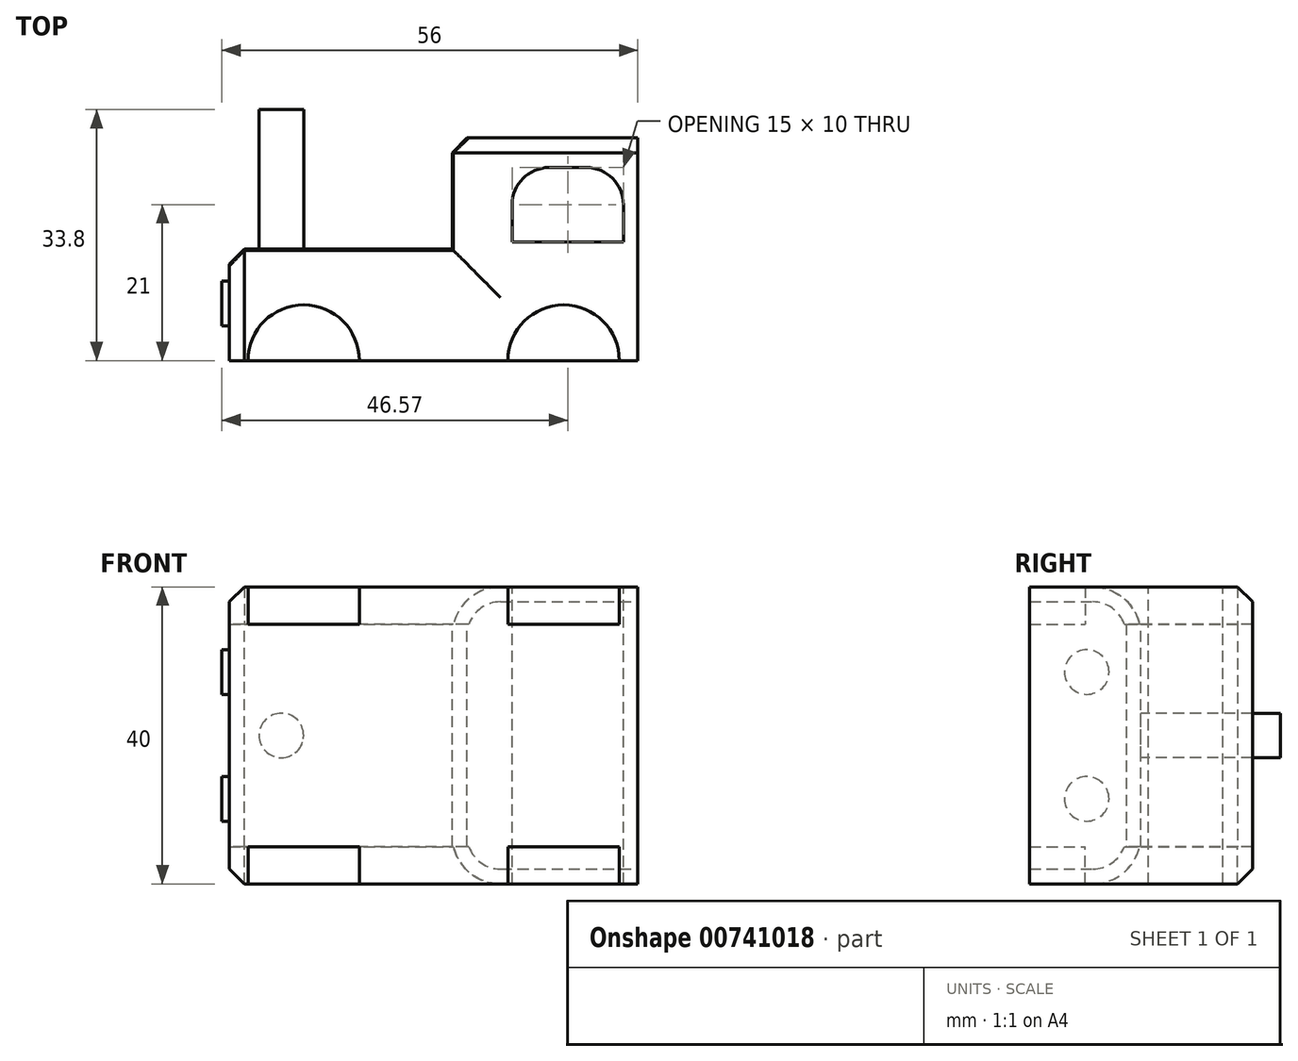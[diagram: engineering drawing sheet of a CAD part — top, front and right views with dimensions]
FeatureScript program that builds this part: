
annotation { "Feature Type Name" : "Feature", "Feature Type Description" : "" }
export const myFeature = defineFeature(function(context is Context, id is Id, definition is map)
    precondition{}
    {
        {
            var Q0;
            Q0=qCreatedBy(makeId("Top.planeOp"),FACE);
            var sketch = newSketch(context, id + "F0", { "sketchPlane" : qUnion([Q0])});
            skLineSegment(sketch, "E0.bottom", {"start": v(27.5, -15) * mm, "end": v(-27.5, -15) * mm});
            skLineSegment(sketch, "E0.top", {"start": v(27.5, 15) * mm, "end": v(-27.5, 15) * mm});
            skLineSegment(sketch, "E0.left", {"start": v(27.5, -15) * mm, "end": v(27.5, 15) * mm});
            skLineSegment(sketch, "E0.right", {"start": v(-27.5, -15) * mm, "end": v(-27.5, 15) * mm});
            skPoint(sketch, "E0.middle", {"position": v(0, 0) * mm});
            skSolve(sketch);
        }
        {
            var Q0;
            Q0 = qSketchRegion(id + "F0", true);
            extrude(context, id + "F1", {"entities" : qUnion([Q0]), "depth" : 30 * mm, "offsetDistance" : 25.4 * mm, "symmetric" : true});
        }
        {
            var Q0;
            Q0=makeQuery(id+"F1.opExtrude","CAP_FACE",FACE,{"disambiguationData":[OSD([sQuery(id+"F0.wireOp",EDGE,"E0.bottom"),sQuery(id+"F0.wireOp",EDGE,"E0.top"),sQuery(id+"F0.wireOp",EDGE,"E0.left"),sQuery(id+"F0.wireOp",EDGE,"E0.right")])],"isStart":false});
            var sketch = newSketch(context, id + "F2", { "sketchPlane" : qUnion([Q0])});
            skLineSegment(sketch, "E1", {"start": v(-27.5, 0) * mm, "end": v(2.5, 0) * mm});
            skLineSegment(sketch, "E2", {"start": v(2.5, 0) * mm, "end": v(2.5, 15) * mm});
            skSolve(sketch);
        }
        {
            var Q0;
            {var subQ0=sQuery(id+"F2.wireOp",EDGE,"E1");Q0=makeQuery(id+"F2.imprint","IMPRINT",FACE,{"disambiguationData":[TD([[makeQuery(id+"F2.imprint","IMPRINT",EDGE,{"derivedFrom":subQ0}),1.0]])]});}
            extrude(context, id + "F3", {"entities" : qUnion([Q0]), "operationType" : NewBodyOperationType.REMOVE, "endBound" : BoundingType.THROUGH_ALL, "oppositeDirection" : true, "depth" : 3.53 * mm, "offsetDistance" : 25.4 * mm});
        }
        {
            var Q0;
            Q0=makeQuery(id+"F1.opExtrude","CAP_FACE",FACE,{"disambiguationData":[OSD([sQuery(id+"F0.wireOp",EDGE,"E0.bottom"),sQuery(id+"F0.wireOp",EDGE,"E0.top"),sQuery(id+"F0.wireOp",EDGE,"E0.left"),sQuery(id+"F0.wireOp",EDGE,"E0.right")])],"isStart":false});
            var sketch = newSketch(context, id + "F4", { "sketchPlane" : qUnion([Q0])});
            skCircle(sketch, "E3", {"center": v(-17.5, -15) * mm, "radius": 7.5 * mm});
            skCircle(sketch, "E4.1.0.0", {"center": v(17.5, -15) * mm, "radius": 7.5 * mm});
            skLineSegment(sketch, "E4.direction1", {"start": v(-17.5, -15) * mm, "end": v(17.5, -15) * mm, "construction": true});
            skSolve(sketch);
        }
        {
            var Q0;
            {var subQ0=makeQuery(id+"F1.opExtrude","CAP_EDGE",EDGE,{"disambiguationData":[OSD([sQuery(id+"F0.wireOp",EDGE,"E0.left")])],"isStart":false});Q0=makeQuery(id+"F4.imprint","IMPRINT",FACE,{"disambiguationData":[TD([[makeQuery(id+"F4.imprint","IMPRINT",EDGE,{"derivedFrom":subQ0}),1.0]])]});}
            extrude(context, id + "F5", {"entities" : qUnion([Q0]), "operationType" : NewBodyOperationType.ADD, "depth" : 5 * mm, "offsetDistance" : 25.4 * mm});
        }
        {
            var Q0;
            Q0=makeQuery(id+"F5.opExtrude","CAP_EDGE",EDGE,{"disambiguationData":[OSD([sQuery(id+"F2.wireOp",EDGE,"E1")])],"isStart":false});
            var Q1;
            Q1=makeQuery(id+"FCjg2uL26yfeYgk_1.1.F5.opExtrude","CAP_EDGE",EDGE,{"disambiguationData":[OSD([sQuery(id+"F2.wireOp",EDGE,"E1")])],"isStart":false});
            var Q2;
            Q2=makeQuery(id+"F5.opExtrude","CAP_EDGE",EDGE,{"disambiguationData":[OSD([sQuery(id+"F2.wireOp",EDGE,"E2")])],"isStart":false});
            var Q3;
            Q3=makeQuery(id+"FCjg2uL26yfeYgk_1.1.F5.opExtrude","CAP_EDGE",EDGE,{"disambiguationData":[OSD([sQuery(id+"F2.wireOp",EDGE,"E2")])],"isStart":false});
            fillet(context, id + "F6", {"entities" : qUnion([Q0, Q1, Q2, Q3]), "radius" : 6.5 * mm, "tangentPropagation" : true, "allowEdgeOverflow" : false});
        }
        {
            var Q0;
            {var subQ0=sQuery(id+"F2.wireOp",EDGE,"E2");var subQ1=sQuery(id+"F0.wireOp",EDGE,"E0.top");Q0=makeQuery(id+"FCjg2uL26yfeYgk_1.1.F5.boolean.opBoolean","MERGE",EDGE,{"derivedFrom":[makeQuery(id+"F5.boolean.opBoolean","MERGE",EDGE,{"derivedFrom":[makeQuery(id+"F3.boolean.opBoolean","COPY",EDGE,{"derivedFrom":makeQuery(id+"F3.opExtrude","SWEPT_EDGE",EDGE,{"disambiguationData":[OSD([subQ1,subQ0])]})}),makeQuery(id+"F5.opExtrude","SWEPT_EDGE",EDGE,{"disambiguationData":[OSD([subQ1,subQ0])]})]}),makeQuery(id+"FCjg2uL26yfeYgk_1.1.F5.opExtrude","SWEPT_EDGE",EDGE,{"disambiguationData":[OSD([subQ1,subQ0])]})]});}
            var Q1;
            {var subQ0=sQuery(id+"F2.wireOp",EDGE,"E1");var subQ1=sQuery(id+"F0.wireOp",EDGE,"E0.right");Q1=makeQuery(id+"FCjg2uL26yfeYgk_1.1.F5.boolean.opBoolean","MERGE",EDGE,{"derivedFrom":[makeQuery(id+"F5.boolean.opBoolean","MERGE",EDGE,{"derivedFrom":[makeQuery(id+"F3.boolean.opBoolean","COPY",EDGE,{"derivedFrom":makeQuery(id+"F3.opExtrude","SWEPT_EDGE",EDGE,{"disambiguationData":[OSD([subQ1,subQ0])]})}),makeQuery(id+"F5.opExtrude","SWEPT_EDGE",EDGE,{"disambiguationData":[OSD([subQ1,subQ0])]})]}),makeQuery(id+"FCjg2uL26yfeYgk_1.1.F5.opExtrude","SWEPT_EDGE",EDGE,{"disambiguationData":[OSD([subQ1,subQ0])]})]});}
            var Q2;
            Q2=makeQuery(id+"F5.opExtrude","CAP_EDGE",EDGE,{"disambiguationData":[OSD([sQuery(id+"F0.wireOp",EDGE,"E0.top")])],"isStart":false});
            var Q3;
            Q3=makeQuery(id+"FCjg2uL26yfeYgk_1.1.F5.opExtrude","CAP_EDGE",EDGE,{"disambiguationData":[OSD([sQuery(id+"F0.wireOp",EDGE,"E0.top")])],"isStart":false});
            chamfer(context, id + "F7", {"entities" : qUnion([Q0, Q1, Q2, Q3]), "width" : 2 * mm, "tangentPropagation" : true});
        }
        {
            var Q0;
            Q0=makeQuery(id+"F5.opExtrude","CAP_FACE",FACE,{"disambiguationData":[OSD([sQuery(id+"F0.wireOp",EDGE,"E0.bottom"),sQuery(id+"F0.wireOp",EDGE,"E0.top"),sQuery(id+"F0.wireOp",EDGE,"E0.left"),sQuery(id+"F0.wireOp",EDGE,"E0.right"),sQuery(id+"F2.wireOp",EDGE,"E1"),sQuery(id+"F2.wireOp",EDGE,"E2"),sQuery(id+"F4.wireOp",EDGE,"E3"),sQuery(id+"F4.wireOp",EDGE,"E4.1.0.0")])],"isStart":false});
            var sketch = newSketch(context, id + "F8", { "sketchPlane" : qUnion([Q0])});
            skLineSegment(sketch, "E5.bottom", {"start": v(10.57, 11) * mm, "end": v(25.57, 11) * mm});
            skLineSegment(sketch, "E5.top", {"start": v(10.57, 1) * mm, "end": v(25.57, 1) * mm});
            skLineSegment(sketch, "E5.left", {"start": v(10.57, 11) * mm, "end": v(10.57, 1) * mm});
            skLineSegment(sketch, "E5.right", {"start": v(25.57, 11) * mm, "end": v(25.57, 1) * mm});
            skSolve(sketch);
        }
        {
            var Q0;
            Q0=makeQuery(id+"F8.imprint","IMPRINT",FACE,{"disambiguationData":[TD([[makeQuery(id+"F8.imprint","IMPRINT",EDGE,{"derivedFrom":sQuery(id+"F8.wireOp",EDGE,"E5.bottom")}),-1.0]])]});
            extrude(context, id + "F9", {"entities" : qUnion([Q0]), "operationType" : NewBodyOperationType.REMOVE, "endBound" : BoundingType.THROUGH_ALL, "oppositeDirection" : true, "depth" : 25.4 * mm, "offsetDistance" : 25.4 * mm});
        }
        {
            var Q0;
            Q0=makeQuery(id+"F9.boolean.opBoolean","COPY",EDGE,{"derivedFrom":makeQuery(id+"F9.opExtrude","SWEPT_EDGE",EDGE,{"disambiguationData":[OSD([sQuery(id+"F8.wireOp",EDGE,"E5.bottom"),sQuery(id+"F8.wireOp",EDGE,"E5.left")])]})});
            var Q1;
            Q1=makeQuery(id+"F9.boolean.opBoolean","COPY",EDGE,{"derivedFrom":makeQuery(id+"F9.opExtrude","SWEPT_EDGE",EDGE,{"disambiguationData":[OSD([sQuery(id+"F8.wireOp",EDGE,"E5.bottom"),sQuery(id+"F8.wireOp",EDGE,"E5.right")])]})});
            fillet(context, id + "F10", {"entities" : qUnion([Q0, Q1]), "radius" : 5 * mm, "tangentPropagation" : true, "allowEdgeOverflow" : false});
        }
        {
            var Q0;
            {var subQ0=sQuery(id+"F0.wireOp",EDGE,"E0.right");Q0=makeQuery(id+"FCjg2uL26yfeYgk_1.1.F5.boolean.opBoolean","MERGE",FACE,{"derivedFrom":[makeQuery(id+"F5.boolean.opBoolean","MERGE",FACE,{"derivedFrom":[makeQuery(id+"F1.opExtrude","SWEPT_FACE",FACE,{"disambiguationData":[OSD([subQ0])]}),makeQuery(id+"F5.opExtrude","SWEPT_FACE",FACE,{"disambiguationData":[OSD([subQ0])]})]}),makeQuery(id+"FCjg2uL26yfeYgk_1.1.F5.opExtrude","SWEPT_FACE",FACE,{"disambiguationData":[OSD([subQ0])]})]});}
            var sketch = newSketch(context, id + "F11", { "sketchPlane" : qUnion([Q0])});
            skCircle(sketch, "E6", {"center": v(7.3, -8.54) * mm, "radius": 3 * mm});
            skPoint(sketch, "E6.first.point", {"position": v(6.98, -11.53) * mm});
            skPoint(sketch, "E6.second.point", {"position": v(10.21, -7.8) * mm});
            skPoint(sketch, "E6.third.point", {"position": v(8.27, -5.7) * mm});
            skSolve(sketch);
        }
        {
            var Q0;
            Q0=makeQuery(id+"F11.imprint","IMPRINT",FACE,{"disambiguationData":[TD([[makeQuery(id+"F11.imprint","IMPRINT",EDGE,{"derivedFrom":sQuery(id+"F11.wireOp",EDGE,"E6")}),1.0]])]});
            extrude(context, id + "F12", {"entities" : qUnion([Q0]), "operationType" : NewBodyOperationType.ADD, "depth" : 1 * mm, "offsetDistance" : 25.4 * mm});
        }
        {
            var Q0;
            Q0=makeQuery(id+"F1.opExtrude","SWEPT_BODY",BODY,{"disambiguationData":[OSD([sQuery(id+"F0.wireOp",EDGE,"E0.bottom"),sQuery(id+"F0.wireOp",EDGE,"E0.top"),sQuery(id+"F0.wireOp",EDGE,"E0.left"),sQuery(id+"F0.wireOp",EDGE,"E0.right")])]});
            var Q1;
            Q1=qCreatedBy(makeId("Top.planeOp"),FACE);
            mirror(context, id + "F13", {"operationType" : NewBodyOperationType.ADD, "entities" : qUnion([Q0]), "mirrorPlane" : qUnion([Q1])});
        }
        {
            var Q0;
            {var subQ0=sQuery(id+"F2.wireOp",EDGE,"E1");Q0=makeQuery(id+"FCjg2uL26yfeYgk_1.1.F5.boolean.opBoolean","MERGE",FACE,{"derivedFrom":[makeQuery(id+"F5.boolean.opBoolean","MERGE",FACE,{"derivedFrom":[makeQuery(id+"F3.boolean.opBoolean","COPY",FACE,{"derivedFrom":makeQuery(id+"F3.opExtrude","SWEPT_FACE",FACE,{"disambiguationData":[OSD([subQ0])]})}),makeQuery(id+"F5.opExtrude","SWEPT_FACE",FACE,{"disambiguationData":[OSD([subQ0])]})]}),makeQuery(id+"FCjg2uL26yfeYgk_1.1.F5.opExtrude","SWEPT_FACE",FACE,{"disambiguationData":[OSD([subQ0])]})]});}
            var sketch = newSketch(context, id + "F14", { "sketchPlane" : qUnion([Q0])});
            skCircle(sketch, "E7", {"center": v(20.5, 0) * mm, "radius": 3 * mm});
            skSolve(sketch);
        }
        {
            var Q0;
            Q0=makeQuery(id+"F14.imprint","IMPRINT",FACE,{"disambiguationData":[TD([[makeQuery(id+"F14.imprint","IMPRINT",EDGE,{"derivedFrom":sQuery(id+"F14.wireOp",EDGE,"E7")}),1.0]])]});
            extrude(context, id + "F15", {"entities" : qUnion([Q0]), "operationType" : NewBodyOperationType.ADD, "depth" : 18.8 * mm, "offsetDistance" : 25.4 * mm});
        }
    });
